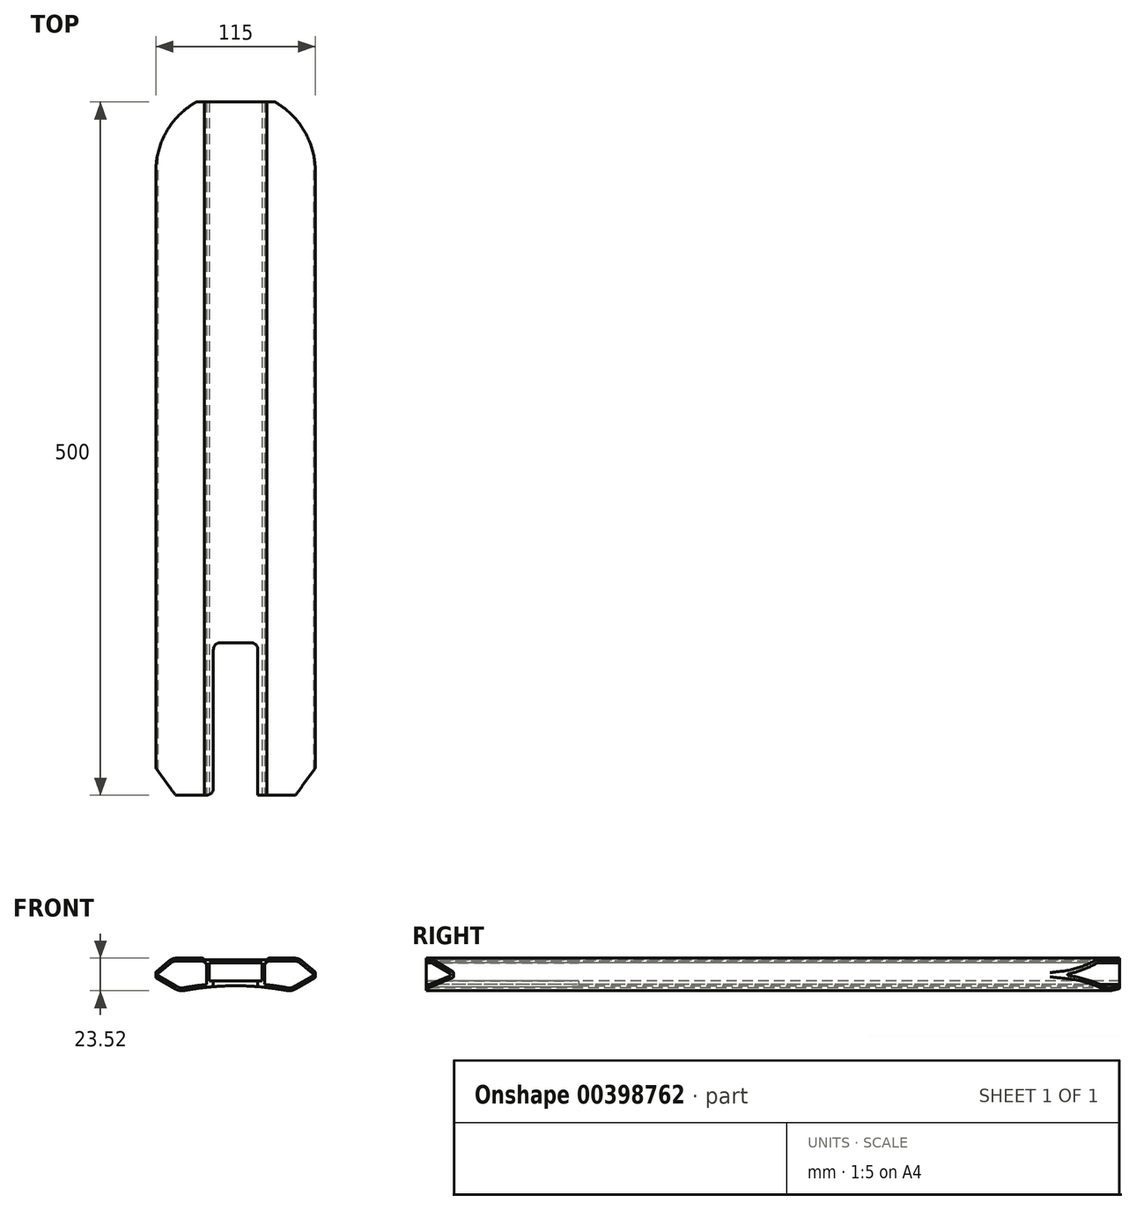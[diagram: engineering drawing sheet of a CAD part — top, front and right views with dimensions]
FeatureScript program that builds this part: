
annotation { "Feature Type Name" : "Feature", "Feature Type Description" : "" }
export const myFeature = defineFeature(function(context is Context, id is Id, definition is map)
    precondition{}
    {
        {
            var Q0;
            Q0=qCreatedBy(makeId("Front.planeOp"),FACE);
            var sketch = newSketch(context, id + "F0", { "sketchPlane" : qUnion([Q0])});
            skLineSegment(sketch, "E0", {"start": v(0, 14.74) * mm, "end": v(0, 0) * mm});
            skLineSegment(sketch, "E1", {"start": v(0, 11.74) * mm, "end": v(22.5, 11.74) * mm});
            skLineSegment(sketch, "E2", {"start": v(22.5, 11.74) * mm, "end": v(22.5, 13.04) * mm});
            skLineSegment(sketch, "E3", {"start": v(22.5, 13.04) * mm, "end": v(45.58, 13.04) * mm});
            skLineSegment(sketch, "E4", {"start": v(45.58, 13.04) * mm, "end": v(57.5, 3.04) * mm});
            skLineSegment(sketch, "E5", {"start": v(57.5, 3.04) * mm, "end": v(57.5, -0.96) * mm});
            skLineSegment(sketch, "E6", {"start": v(57.5, -0.96) * mm, "end": v(40.18, -10.96) * mm});
            skLineSegment(sketch, "E7.MirrorCS", {"start": v(0, 11.74) * mm, "end": v(-22.5, 11.74) * mm});
            skLineSegment(sketch, "E8.MirrorCS", {"start": v(-22.5, 13.04) * mm, "end": v(-45.58, 13.04) * mm});
            skLineSegment(sketch, "E9.MirrorCS", {"start": v(-57.5, -0.96) * mm, "end": v(-40.18, -10.96) * mm});
            skLineSegment(sketch, "E10.MirrorCS", {"start": v(-22.5, 11.74) * mm, "end": v(-22.5, 13.04) * mm});
            skLineSegment(sketch, "E11.MirrorCS", {"start": v(-45.58, 13.04) * mm, "end": v(-57.5, 3.04) * mm});
            skLineSegment(sketch, "E12.MirrorCS", {"start": v(-57.5, 3.04) * mm, "end": v(-57.5, -0.96) * mm});
            skArc(sketch, "E13", {"start": v(40.18, -10.96) * mm, "mid": v(0, -6.89) * mm, "end": v(-40.18, -10.96) * mm});
            skSolve(sketch);
        }
        {
            var Q0;
            Q0=makeQuery(id+"F0.imprint","IMPRINT",FACE,{"disambiguationData":[TD([[makeQuery(id+"F0.imprint","IMPRINT",EDGE,{"derivedFrom":sQuery(id+"F0.wireOp",EDGE,"E1")}),-1.0]])]});
            extrude(context, id + "F1", {"entities" : qUnion([Q0]), "endBound" : BoundingType.SYMMETRIC, "depth" : 500 * mm});
        }
        {
            var Q0;
            Q0=qCreatedBy(makeId("Front.planeOp"),FACE);
            var sketch = newSketch(context, id + "F2", { "sketchPlane" : qUnion([Q0])});
            skLineSegment(sketch, "E14.bottom", {"start": v(19, -3.26) * mm, "end": v(-19, -3.26) * mm});
            skLineSegment(sketch, "E14.top", {"start": v(19, 9.74) * mm, "end": v(-19, 9.74) * mm});
            skLineSegment(sketch, "E14.left", {"start": v(19, -3.26) * mm, "end": v(19, 9.74) * mm});
            skLineSegment(sketch, "E14.right", {"start": v(-19, -3.26) * mm, "end": v(-19, 9.74) * mm});
            skSolve(sketch);
        }
        {
            var Q0;
            Q0=qSketchRegion(id+"F2",true);
            extrude(context, id + "F3", {"entities" : qUnion([Q0]), "operationType" : NewBodyOperationType.REMOVE, "endBound" : BoundingType.SYMMETRIC, "oppositeDirection" : true, "depth" : 500 * mm});
        }
        {
            var Q0;
            Q0=makeQuery(id+"F1.opExtrude","SWEPT_EDGE",EDGE,{"disambiguationData":[OSD([sQuery(id+"F0.wireOp",EDGE,"E8.MirrorCS"),sQuery(id+"F0.wireOp",EDGE,"E10.MirrorCS")])]});
            var Q1;
            Q1=makeQuery(id+"F1.opExtrude","SWEPT_EDGE",EDGE,{"disambiguationData":[OSD([sQuery(id+"F0.wireOp",EDGE,"E2"),sQuery(id+"F0.wireOp",EDGE,"E3")])]});
            fillet(context, id + "F4", {"entities" : qUnion([Q0, Q1]), "radius" : 2 * mm, "tangentPropagation" : true, "allowEdgeOverflow" : false});
        }
        {
            var Q0;
            Q0=makeQuery(id+"F1.opExtrude","SWEPT_EDGE",EDGE,{"disambiguationData":[OSD([sQuery(id+"F0.wireOp",EDGE,"E8.MirrorCS"),sQuery(id+"F0.wireOp",EDGE,"E11.MirrorCS")])]});
            var Q1;
            Q1=makeQuery(id+"F1.opExtrude","SWEPT_EDGE",EDGE,{"disambiguationData":[OSD([sQuery(id+"F0.wireOp",EDGE,"E3"),sQuery(id+"F0.wireOp",EDGE,"E4")])]});
            var Q2;
            Q2=makeQuery(id+"F1.opExtrude","SWEPT_EDGE",EDGE,{"disambiguationData":[OSD([sQuery(id+"F0.wireOp",EDGE,"E9.MirrorCS"),sQuery(id+"F0.wireOp",EDGE,"E13")])]});
            var Q3;
            Q3=makeQuery(id+"F1.opExtrude","SWEPT_EDGE",EDGE,{"disambiguationData":[OSD([sQuery(id+"F0.wireOp",EDGE,"E6"),sQuery(id+"F0.wireOp",EDGE,"E13")])]});
            fillet(context, id + "F5", {"entities" : qUnion([Q0, Q1, Q2, Q3]), "radius" : 9 * mm, "tangentPropagation" : true, "allowEdgeOverflow" : false});
        }
        {
            var Q0;
            Q0=makeQuery(id+"F1.opExtrude","SWEPT_EDGE",EDGE,{"disambiguationData":[OSD([sQuery(id+"F0.wireOp",EDGE,"E4"),sQuery(id+"F0.wireOp",EDGE,"E5")])]});
            var Q1;
            Q1=makeQuery(id+"F1.opExtrude","SWEPT_EDGE",EDGE,{"disambiguationData":[OSD([sQuery(id+"F0.wireOp",EDGE,"E5"),sQuery(id+"F0.wireOp",EDGE,"E6")])]});
            var Q2;
            Q2=makeQuery(id+"F1.opExtrude","SWEPT_EDGE",EDGE,{"disambiguationData":[OSD([sQuery(id+"F0.wireOp",EDGE,"E11.MirrorCS"),sQuery(id+"F0.wireOp",EDGE,"E12.MirrorCS")])]});
            var Q3;
            Q3=makeQuery(id+"F1.opExtrude","SWEPT_EDGE",EDGE,{"disambiguationData":[OSD([sQuery(id+"F0.wireOp",EDGE,"E9.MirrorCS"),sQuery(id+"F0.wireOp",EDGE,"E12.MirrorCS")])]});
            fillet(context, id + "F6", {"entities" : qUnion([Q0, Q1, Q2, Q3]), "radius" : 1 * mm, "tangentPropagation" : true, "allowEdgeOverflow" : false});
        }
        {
            var Q0;
            Q0=makeQuery(id+"F1.opExtrude","CAP_FACE",FACE,{"disambiguationData":[OSD([sQuery(id+"F0.wireOp",EDGE,"E1"),sQuery(id+"F0.wireOp",EDGE,"E2"),sQuery(id+"F0.wireOp",EDGE,"E3"),sQuery(id+"F0.wireOp",EDGE,"E4"),sQuery(id+"F0.wireOp",EDGE,"E5"),sQuery(id+"F0.wireOp",EDGE,"E6"),sQuery(id+"F0.wireOp",EDGE,"E7.MirrorCS"),sQuery(id+"F0.wireOp",EDGE,"E8.MirrorCS"),sQuery(id+"F0.wireOp",EDGE,"E9.MirrorCS"),sQuery(id+"F0.wireOp",EDGE,"E10.MirrorCS"),sQuery(id+"F0.wireOp",EDGE,"E11.MirrorCS"),sQuery(id+"F0.wireOp",EDGE,"E12.MirrorCS"),sQuery(id+"F0.wireOp",EDGE,"E13")])],"isStart":false});
            var sketch = newSketch(context, id + "F7", { "sketchPlane" : qUnion([Q0])});
            skArc(sketch, "E15.0", {"start": v(-37.3, -8.36) * mm, "mid": v(-29.18, -7) * mm, "end": v(-21, -5.98) * mm});
            skArc(sketch, "E15.1", {"start": v(-42.1, -7.54) * mm, "mid": v(-39.78, -8.38) * mm, "end": v(-37.3, -8.36) * mm});
            skLineSegment(sketch, "E15.2", {"start": v(-24.37, 11.04) * mm, "end": v(-42.3, 11.04) * mm});
            skArc(sketch, "E15.3", {"start": v(-42.3, 11.04) * mm, "mid": v(-44.7, 10.61) * mm, "end": v(-46.8, 9.4) * mm});
            skLineSegment(sketch, "E15.4", {"start": v(-46.8, 9.4) * mm, "end": v(-55.76, 1.89) * mm});
            skLineSegment(sketch, "E15.5", {"start": v(-55.61, 0.26) * mm, "end": v(-42.1, -7.54) * mm});
            skPoint(sketch, "E16.visualSharp", {"position": v(-56.85, 0.97) * mm});
            skArc(sketch, "E16.filletArc", {"start": v(-55.76, 1.89) * mm, "mid": v(-56.1, 1.04) * mm, "end": v(-55.61, 0.26) * mm});
            skLineSegment(sketch, "E17", {"start": v(-21, -5.98) * mm, "end": v(-21, 9.74) * mm});
            skLineSegment(sketch, "E18", {"start": v(-21, 9.74) * mm, "end": v(-22.5, 9.74) * mm});
            skArc(sketch, "E19", {"start": v(-22.5, 9.74) * mm, "mid": v(-23.23, 10.68) * mm, "end": v(-24.37, 11.04) * mm});
            skLineSegment(sketch, "E20.MirrorCS", {"start": v(46.8, 9.4) * mm, "end": v(55.76, 1.89) * mm});
            skArc(sketch, "E21.MirrorCS", {"start": v(42.3, 11.04) * mm, "mid": v(44.7, 10.61) * mm, "end": v(46.8, 9.4) * mm});
            skLineSegment(sketch, "E22.MirrorCS", {"start": v(55.61, 0.26) * mm, "end": v(42.1, -7.54) * mm});
            skLineSegment(sketch, "E23.MirrorCS", {"start": v(24.37, 11.04) * mm, "end": v(42.3, 11.04) * mm});
            skArc(sketch, "E24.MirrorCS", {"start": v(42.1, -7.54) * mm, "mid": v(39.78, -8.38) * mm, "end": v(37.3, -8.36) * mm});
            skLineSegment(sketch, "E25.MirrorCS", {"start": v(21, -5.98) * mm, "end": v(21, 9.74) * mm});
            skLineSegment(sketch, "E26.MirrorCS", {"start": v(21, 9.74) * mm, "end": v(22.5, 9.74) * mm});
            skArc(sketch, "E27.MirrorCS", {"start": v(22.5, 9.74) * mm, "mid": v(23.23, 10.68) * mm, "end": v(24.37, 11.04) * mm});
            skArc(sketch, "E28.MirrorCS", {"start": v(55.76, 1.89) * mm, "mid": v(56.1, 1.04) * mm, "end": v(55.61, 0.26) * mm});
            skArc(sketch, "E29.trimOffspring", {"start": v(21, -5.98) * mm, "mid": v(29.18, -7) * mm, "end": v(37.3, -8.36) * mm});
            skPoint(sketch, "E30.0.16.end.orphan", {"position": v(22.5, 11.74) * mm});
            skPoint(sketch, "E30.0.0.start.orphan", {"position": v(-42.3, 13.04) * mm});
            skPoint(sketch, "E30.0.6.end.orphan", {"position": v(-36.94, -10.33) * mm});
            skPoint(sketch, "E30.0.5.end.orphan", {"position": v(-43.1, -9.28) * mm});
            skPoint(sketch, "E30.0.4.end.orphan", {"position": v(-57, -1.25) * mm});
            skPoint(sketch, "E30.0.3.end.orphan", {"position": v(-57.5, -0.39) * mm});
            skPoint(sketch, "E30.0.2.end.orphan", {"position": v(-57.5, 2.57) * mm});
            skSolve(sketch);
        }
        {
            var Q0;
            Q0=qSketchRegion(id+"F7",true);
            extrude(context, id + "F8", {"entities" : qUnion([Q0]), "operationType" : NewBodyOperationType.REMOVE, "endBound" : BoundingType.THROUGH_ALL, "oppositeDirection" : true, "depth" : 500 * mm});
        }
        {
            var Q0;
            Q0=qCreatedBy(makeId("Top.planeOp"),FACE);
            var sketch = newSketch(context, id + "F9", { "sketchPlane" : qUnion([Q0])});
            skArc(sketch, "E31", {"start": v(57.5, 200) * mm, "mid": v(0, 257.5) * mm, "end": v(-57.5, 200) * mm});
            skLineSegment(sketch, "E32", {"start": v(57.5, 200) * mm, "end": v(57.5, 280) * mm});
            skLineSegment(sketch, "E33", {"start": v(57.5, 280) * mm, "end": v(-57.5, 280) * mm});
            skLineSegment(sketch, "E34", {"start": v(-57.5, 280) * mm, "end": v(-57.5, 200) * mm});
            skSolve(sketch);
        }
        {
            var Q0;
            Q0=qSketchRegion(id+"F9",true);
            extrude(context, id + "F10", {"entities" : qUnion([Q0]), "operationType" : NewBodyOperationType.REMOVE, "endBound" : BoundingType.THROUGH_ALL, "oppositeDirection" : true, "depth" : 25 * mm, "hasSecondDirection" : true, "secondDirectionBound" : SecondDirectionBoundingType.THROUGH_ALL, "secondDirectionOppositeDirection" : false, "secondDirectionDepth" : 25 * mm});
        }
        {
            var Q0;
            Q0=qCreatedBy(makeId("Top.planeOp"),FACE);
            var sketch = newSketch(context, id + "F11", { "sketchPlane" : qUnion([Q0])});
            skLineSegment(sketch, "E35", {"start": v(-16, -140) * mm, "end": v(16, -140) * mm});
            skLineSegment(sketch, "E36", {"start": v(16, -140) * mm, "end": v(16, -250) * mm});
            skLineSegment(sketch, "E37", {"start": v(16, -250) * mm, "end": v(43.3, -250) * mm});
            skLineSegment(sketch, "E38", {"start": v(43.3, -250) * mm, "end": v(68, -216) * mm});
            skLineSegment(sketch, "E39", {"start": v(68, -216) * mm, "end": v(68, -346) * mm});
            skLineSegment(sketch, "E40", {"start": v(68, -346) * mm, "end": v(-68, -346) * mm});
            skLineSegment(sketch, "E41", {"start": v(-68, -346) * mm, "end": v(-68, -216) * mm});
            skLineSegment(sketch, "E42", {"start": v(-68, -216) * mm, "end": v(-43.3, -250) * mm});
            skLineSegment(sketch, "E43", {"start": v(-43.3, -250) * mm, "end": v(-16, -250) * mm});
            skLineSegment(sketch, "E44", {"start": v(-16, -250) * mm, "end": v(-16, -140) * mm});
            skSolve(sketch);
        }
        {
            var Q0;
            Q0=qSketchRegion(id+"F11",true);
            extrude(context, id + "F12", {"entities" : qUnion([Q0]), "operationType" : NewBodyOperationType.REMOVE, "endBound" : BoundingType.THROUGH_ALL, "depth" : 25 * mm, "hasSecondDirection" : true, "secondDirectionBound" : SecondDirectionBoundingType.THROUGH_ALL, "secondDirectionOppositeDirection" : true, "secondDirectionDepth" : 25 * mm});
        }
        {
            var Q0;
            {var subQ2=sQuery(id+"F11.wireOp",EDGE,"E44");Q0=makeQuery(id+"F12.boolean.opBoolean","COPY",EDGE,{"disambiguationData":[TD([makeQuery(id+"F3.boolean.opBoolean","COPY",FACE,{"derivedFrom":makeQuery(id+"F3.opExtrude","SWEPT_FACE",FACE,{"disambiguationData":[OSD([sQuery(id+"F2.wireOp",EDGE,"E14.top")])]})})])],"derivedFrom":makeQuery(id+"F12.opExtrude","SWEPT_EDGE",EDGE,{"disambiguationData":[OSD([sQuery(id+"F11.wireOp",EDGE,"E43"),subQ2])]})});}
            var Q1;
            {var subQ0=sQuery(id+"F0.wireOp",EDGE,"E13");var subQ1=sQuery(id+"F11.wireOp",EDGE,"E44");Q1=makeQuery(id+"F12.boolean.opBoolean","COPY",EDGE,{"disambiguationData":[TD([makeQuery(id+"F1.opExtrude","SWEPT_FACE",FACE,{"disambiguationData":[OSD([subQ0])]})])],"derivedFrom":makeQuery(id+"F12.opExtrude","SWEPT_EDGE",EDGE,{"disambiguationData":[OSD([sQuery(id+"F11.wireOp",EDGE,"E43"),subQ1])]})});}
            var Q2;
            {var subQ0=sQuery(id+"F11.wireOp",EDGE,"E35");var subQ1=sQuery(id+"F11.wireOp",EDGE,"E44");Q2=makeQuery(id+"F12.boolean.opBoolean","COPY",EDGE,{"disambiguationData":[TD([makeQuery(id+"F3.boolean.opBoolean","COPY",FACE,{"derivedFrom":makeQuery(id+"F3.opExtrude","SWEPT_FACE",FACE,{"disambiguationData":[OSD([sQuery(id+"F2.wireOp",EDGE,"E14.top")])]})})])],"derivedFrom":makeQuery(id+"F12.opExtrude","SWEPT_EDGE",EDGE,{"disambiguationData":[OSD([subQ0,subQ1])]})});}
            var Q3;
            {var subQ0=sQuery(id+"F11.wireOp",EDGE,"E35");var subQ1=sQuery(id+"F11.wireOp",EDGE,"E44");Q3=makeQuery(id+"F12.boolean.opBoolean","COPY",EDGE,{"disambiguationData":[TD([makeQuery(id+"F1.opExtrude","SWEPT_FACE",FACE,{"disambiguationData":[OSD([sQuery(id+"F0.wireOp",EDGE,"E13")])]})])],"derivedFrom":makeQuery(id+"F12.opExtrude","SWEPT_EDGE",EDGE,{"disambiguationData":[OSD([subQ0,subQ1])]})});}
            var Q4;
            {var subQ0=sQuery(id+"F11.wireOp",EDGE,"E35");var subQ1=sQuery(id+"F11.wireOp",EDGE,"E36");Q4=makeQuery(id+"F12.boolean.opBoolean","COPY",EDGE,{"disambiguationData":[TD([makeQuery(id+"F1.opExtrude","SWEPT_FACE",FACE,{"disambiguationData":[OSD([sQuery(id+"F0.wireOp",EDGE,"E13")])]})])],"derivedFrom":makeQuery(id+"F12.opExtrude","SWEPT_EDGE",EDGE,{"disambiguationData":[OSD([subQ0,subQ1])]})});}
            var Q5;
            {var subQ0=sQuery(id+"F11.wireOp",EDGE,"E35");var subQ1=sQuery(id+"F11.wireOp",EDGE,"E36");Q5=makeQuery(id+"F12.boolean.opBoolean","COPY",EDGE,{"disambiguationData":[TD([makeQuery(id+"F3.boolean.opBoolean","COPY",FACE,{"derivedFrom":makeQuery(id+"F3.opExtrude","SWEPT_FACE",FACE,{"disambiguationData":[OSD([sQuery(id+"F2.wireOp",EDGE,"E14.top")])]})})])],"derivedFrom":makeQuery(id+"F12.opExtrude","SWEPT_EDGE",EDGE,{"disambiguationData":[OSD([subQ0,subQ1])]})});}
            var Q6;
            {var subQ0=sQuery(id+"F0.wireOp",EDGE,"E13");var subQ1=sQuery(id+"F11.wireOp",EDGE,"E36");Q6=makeQuery(id+"F12.boolean.opBoolean","COPY",EDGE,{"disambiguationData":[TD([makeQuery(id+"F1.opExtrude","SWEPT_FACE",FACE,{"disambiguationData":[OSD([subQ0])]})])],"derivedFrom":makeQuery(id+"F12.opExtrude","SWEPT_EDGE",EDGE,{"disambiguationData":[OSD([subQ1,sQuery(id+"F11.wireOp",EDGE,"E37")])]})});}
            var Q7;
            {var subQ2=sQuery(id+"F11.wireOp",EDGE,"E36");Q7=makeQuery(id+"F12.boolean.opBoolean","COPY",EDGE,{"disambiguationData":[TD([makeQuery(id+"F3.boolean.opBoolean","COPY",FACE,{"derivedFrom":makeQuery(id+"F3.opExtrude","SWEPT_FACE",FACE,{"disambiguationData":[OSD([sQuery(id+"F2.wireOp",EDGE,"E14.top")])]})})])],"derivedFrom":makeQuery(id+"F12.opExtrude","SWEPT_EDGE",EDGE,{"disambiguationData":[OSD([subQ2,sQuery(id+"F11.wireOp",EDGE,"E37")])]})});}
            fillet(context, id + "F13", {"entities" : qUnion([Q0, Q1, Q2, Q3, Q4, Q5, Q6, Q7]), "radius" : 5 * mm, "tangentPropagation" : true, "allowEdgeOverflow" : false});
        }
    });
